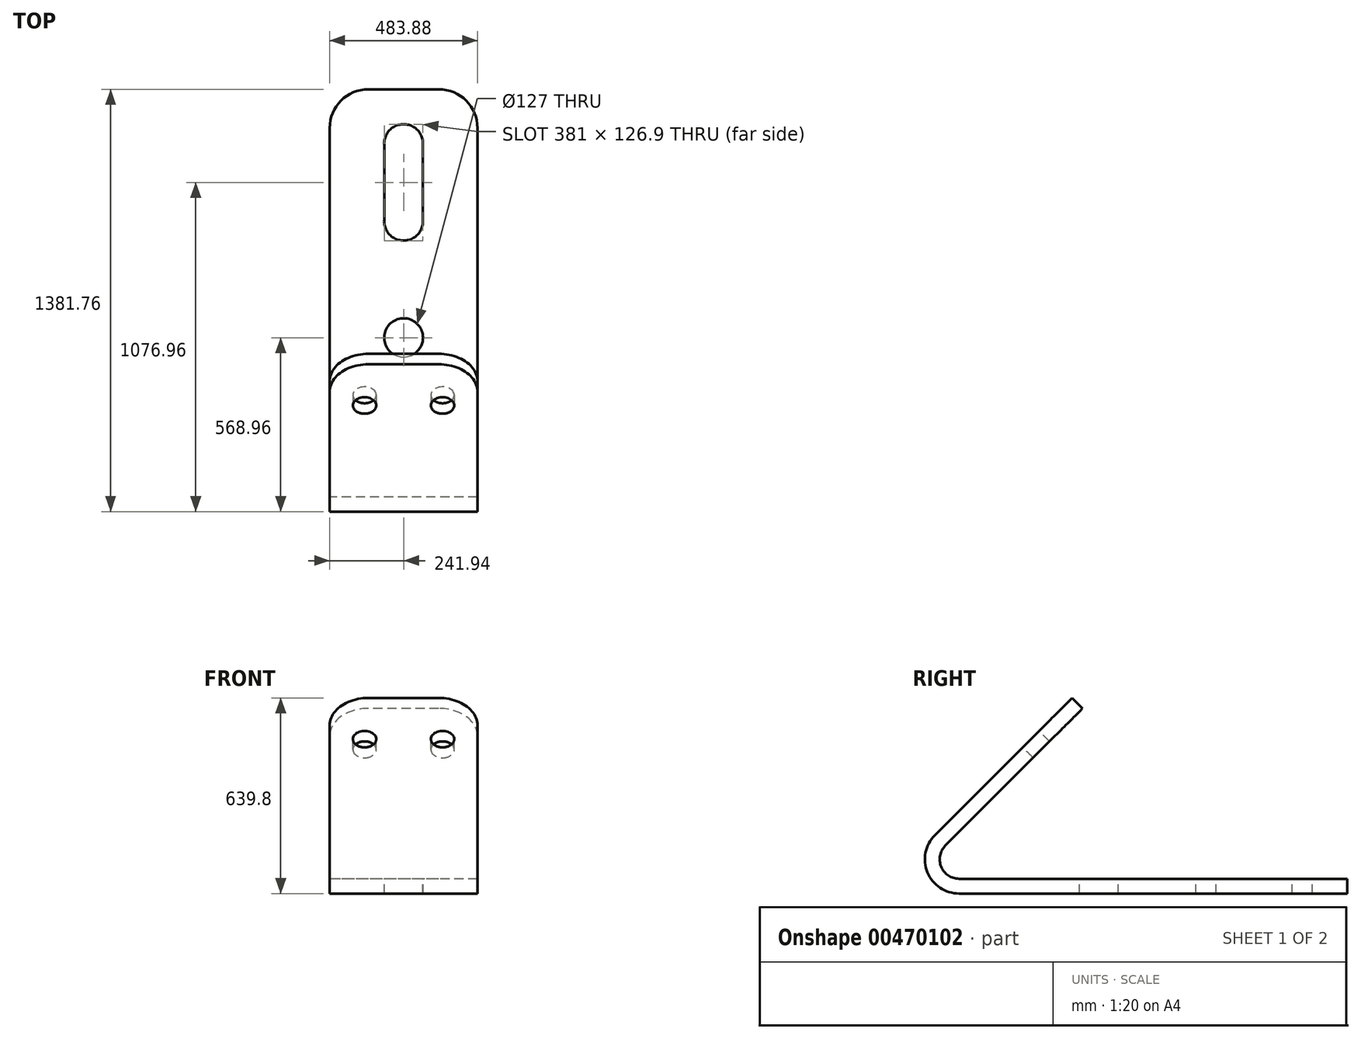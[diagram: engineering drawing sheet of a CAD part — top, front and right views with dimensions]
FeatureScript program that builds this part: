
annotation { "Feature Type Name" : "Feature", "Feature Type Description" : "" }
export const myFeature = defineFeature(function(context is Context, id is Id, definition is map)
    precondition{}
    {
        {
            var Q0;
            Q0=qCreatedBy(makeId("Right.planeOp"),FACE);
            var sketch = newSketch(context, id + "F0", { "sketchPlane" : qUnion([Q0])});
            skLineSegment(sketch, "E0", {"start": v(0, 0) * mm, "end": v(1270, 0) * mm});
            skLineSegment(sketch, "E1", {"start": v(-79.03, 190.79) * mm, "end": v(369.99, 639.8) * mm});
            skArc(sketch, "E2", {"start": v(-79.03, 190.79) * mm, "mid": v(-103.25, 69) * mm, "end": v(0, 0) * mm});
            skPoint(sketch, "E2.third.point", {"position": v(-111.24, 122.56) * mm});
            skLineSegment(sketch, "E3.0", {"start": v(-44.9, 156.66) * mm, "end": v(404.11, 605.67) * mm});
            skArc(sketch, "E3.1", {"start": v(-44.9, 156.66) * mm, "mid": v(-58.67, 87.46) * mm, "end": v(0, 48.26) * mm});
            skLineSegment(sketch, "E3.2", {"start": v(0, 48.26) * mm, "end": v(1270, 48.26) * mm});
            skLineSegment(sketch, "E4", {"start": v(369.99, 639.8) * mm, "end": v(404.11, 605.67) * mm});
            skLineSegment(sketch, "E5", {"start": v(1270, 48.26) * mm, "end": v(1270, 0) * mm});
            skSolve(sketch);
        }
        {
            var Q0;
            Q0 = qSketchRegion(id + "F0", true);
            extrude(context, id + "F1", {"entities" : qUnion([Q0]), "endBound" : BoundingType.SYMMETRIC, "depth" : 483.87 * mm});
        }
        {
            var Q0;
            Q0=makeQuery(id+"F1.opExtrude","SWEPT_FACE",FACE,{"disambiguationData":[OSD([sQuery(id+"F0.wireOp",EDGE,"E3.2")])]});
            var sketch = newSketch(context, id + "F2", { "sketchPlane" : qUnion([Q0])});
            skCircle(sketch, "E6", {"center": v(0, 457.2) * mm, "radius": 63.5 * mm});
            skPoint(sketch, "E6.centerSnap0", {"position": v(0, 1270) * mm});
            skArc(sketch, "E7", {"start": v(63.45, 1089.66) * mm, "mid": v(0, 1155.7) * mm, "end": v(-63.45, 1089.66) * mm});
            skArc(sketch, "E8", {"start": v(-63.45, 840.74) * mm, "mid": v(0, 774.7) * mm, "end": v(63.45, 840.74) * mm});
            skLineSegment(sketch, "E9", {"start": v(-63.45, 1089.66) * mm, "end": v(-63.45, 835.66) * mm});
            skLineSegment(sketch, "E10", {"start": v(63.45, 1089.66) * mm, "end": v(63.45, 838.2) * mm});
            skSolve(sketch);
        }
        {
            var Q0;
            Q0 = qSketchRegion(id + "F2", true);
            extrude(context, id + "F3", {"entities" : qUnion([Q0]), "operationType" : NewBodyOperationType.REMOVE, "oppositeDirection" : true, "depth" : 76.2 * mm});
        }
        {
            var Q0;
            Q0=makeQuery(id+"F1.opExtrude","SWEPT_FACE",FACE,{"disambiguationData":[OSD([sQuery(id+"F0.wireOp",EDGE,"E1")])]});
            var sketch = newSketch(context, id + "F4", { "sketchPlane" : qUnion([Q0])});
            skCircle(sketch, "E11", {"center": v(-127.64, 523.53) * mm, "radius": 38.1 * mm});
            skCircle(sketch, "E12", {"center": v(127.64, 523.53) * mm, "radius": 38.1 * mm});
            skSolve(sketch);
        }
        {
            var Q0;
            Q0 = qSketchRegion(id + "F4", true);
            extrude(context, id + "F5", {"entities" : qUnion([Q0]), "operationType" : NewBodyOperationType.REMOVE, "oppositeDirection" : true, "depth" : 76.2 * mm});
        }
        {
            var Q0;
            Q0=makeQuery(id+"F1.opExtrude","CAP_EDGE",EDGE,{"disambiguationData":[OSD([sQuery(id+"F0.wireOp",EDGE,"E4")])],"isStart":false});
            var Q1;
            Q1=makeQuery(id+"F1.opExtrude","CAP_EDGE",EDGE,{"disambiguationData":[OSD([sQuery(id+"F0.wireOp",EDGE,"E4")])],"isStart":true});
            var Q2;
            Q2=makeQuery(id+"F1.opExtrude","CAP_EDGE",EDGE,{"disambiguationData":[OSD([sQuery(id+"F0.wireOp",EDGE,"E5")])],"isStart":false});
            var Q3;
            Q3=makeQuery(id+"F1.opExtrude","CAP_EDGE",EDGE,{"disambiguationData":[OSD([sQuery(id+"F0.wireOp",EDGE,"E5")])],"isStart":true});
            fillet(context, id + "F6", {"entities" : qUnion([Q0, Q1, Q2, Q3]), "radius" : 127 * mm, "tangentPropagation" : true, "allowEdgeOverflow" : false});
        }
    });
